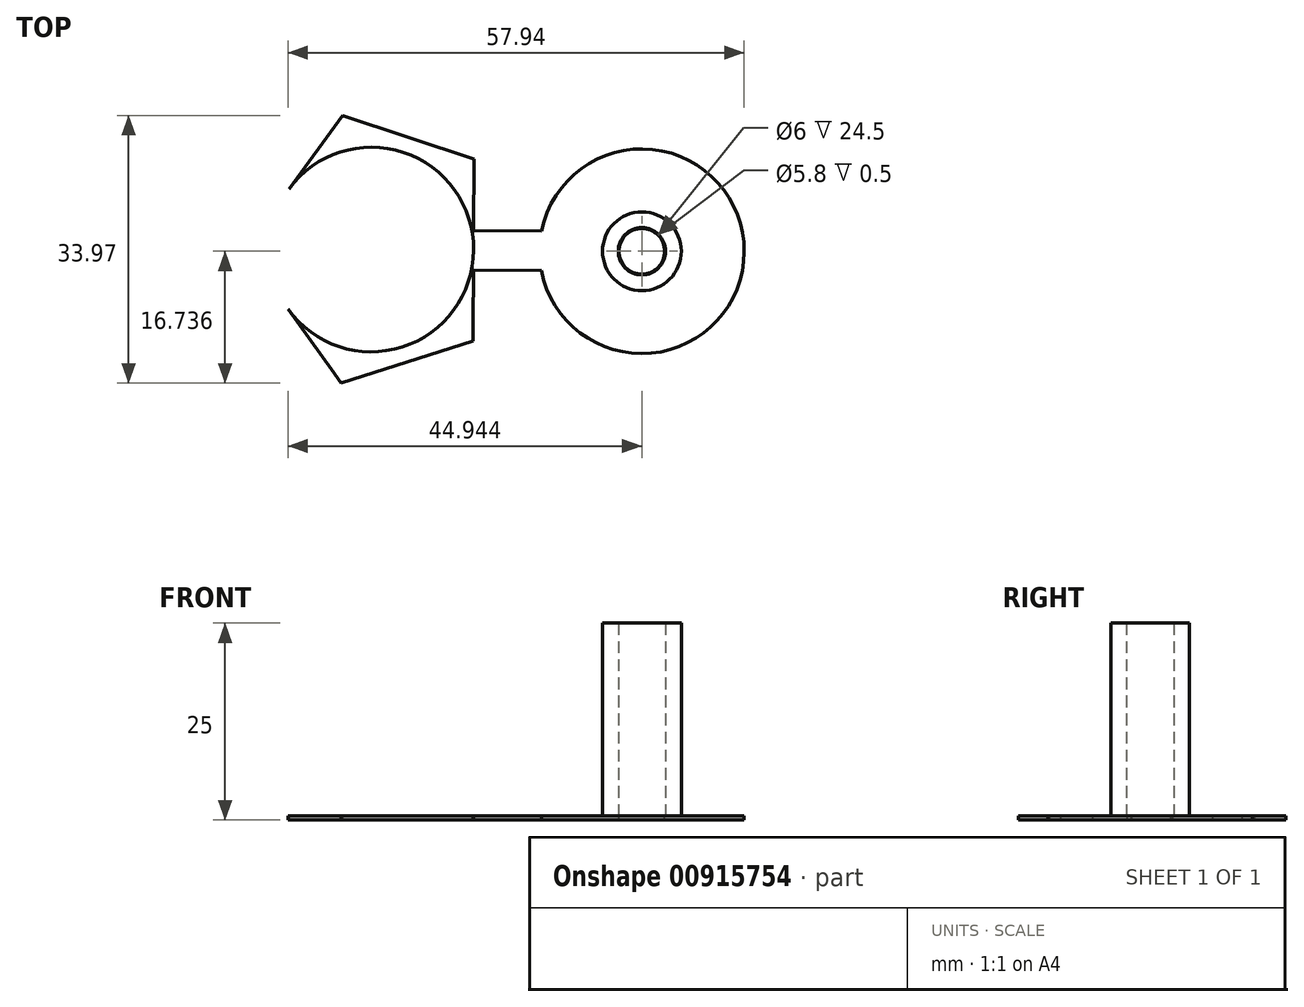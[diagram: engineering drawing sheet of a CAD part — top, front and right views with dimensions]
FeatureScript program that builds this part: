
annotation { "Feature Type Name" : "Feature", "Feature Type Description" : "" }
export const myFeature = defineFeature(function(context is Context, id is Id, definition is map)
    precondition{}
    {
        {
            var Q0;
            Q0=qCreatedBy(makeId("Top.planeOp"),FACE);
            var sketch = newSketch(context, id + "F0", { "sketchPlane" : qUnion([Q0])});
            skCircle(sketch, "E0.cCircle", {"center": v(0, 0) * mm, "radius": 13 * mm, "construction": true});
            skLineSegment(sketch, "E0.0", {"start": v(-4.87, 15.31) * mm, "end": v(13.06, 9.36) * mm});
            skLineSegment(sketch, "E0.1", {"start": v(13.06, 9.36) * mm, "end": v(12.94, -9.53) * mm});
            skLineSegment(sketch, "E0.2", {"start": v(12.94, -9.53) * mm, "end": v(-5.06, -15.25) * mm});
            skLineSegment(sketch, "E0.3", {"start": v(-5.06, -15.25) * mm, "end": v(-16.07, 0.1) * mm});
            skLineSegment(sketch, "E0.4", {"start": v(-16.07, 0.1) * mm, "end": v(-4.87, 15.31) * mm});
            skPoint(sketch, "E0.0.midPoint", {"position": v(4.1, 12.34) * mm});
            skLineSegment(sketch, "E1", {"start": v(12.74, -2.58) * mm, "end": v(34.37, -2.72) * mm});
            skLineSegment(sketch, "E2", {"start": v(34.37, -2.72) * mm, "end": v(34.37, 2.28) * mm});
            skLineSegment(sketch, "E3", {"start": v(34.37, 2.28) * mm, "end": v(12.77, 2.42) * mm});
            skLineSegment(sketch, "E4", {"start": v(0, 0) * mm, "end": v(34.37, -0.22) * mm, "construction": true});
            skCircle(sketch, "E5", {"center": v(34.37, -0.22) * mm, "radius": 13 * mm});
            skCircle(sketch, "E6", {"center": v(0, 0) * mm, "radius": 13 * mm});
            skPoint(sketch, "E7.orphan", {"position": v(0, 2.5) * mm});
            skCircle(sketch, "E8", {"center": v(34.37, -0.22) * mm, "radius": 3 * mm});
            skCircle(sketch, "E9", {"center": v(34.37, -0.22) * mm, "radius": 5 * mm});
            skSolve(sketch);
        }
        {
            var Q0;
            Q0=makeQuery(id+"F0.imprint","IMPRINT",FACE,{"disambiguationData":[TD([[makeQuery(id+"F0.imprint","IMPRINT",EDGE,{"derivedFrom":sQuery(id+"F0.wireOp",EDGE,"E5")}),1.0]])]});
            var Q1;
            {var subQ4=sQuery(id+"F0.wireOp",EDGE,"E0.0");Q1=makeQuery(id+"F0.imprint","IMPRINT",FACE,{"disambiguationData":[TD([[makeQuery(id+"F0.imprint","IMPRINT",EDGE,{"derivedFrom":subQ4}),-1.0]])]});}
            var Q2;
            {var subQ5=sQuery(id+"F0.wireOp",EDGE,"E2");Q2=makeQuery(id+"F0.imprint","IMPRINT",FACE,{"disambiguationData":[TD([[makeQuery(id+"F0.imprint","IMPRINT",EDGE,{"derivedFrom":subQ5}),1.0]])]});}
            var Q3;
            {var subQ5=sQuery(id+"F0.wireOp",EDGE,"jRpVBXlm-WpGf-nScz-VXjb-NFzC1IAMgS5t");Q3=makeQuery(id+"F0.imprint","IMPRINT",FACE,{"disambiguationData":[TD([[makeQuery(id+"F0.imprint","IMPRINT",EDGE,{"derivedFrom":subQ5}),1.0]])]});}
            var Q4;
            {var subQ0=sQuery(id+"F0.wireOp",EDGE,"E0.2");var subQ1=sQuery(id+"F0.wireOp",EDGE,"E0.1");var subQ2=makeQuery(id+"F0.imprint","INTERSECT",VERTEX,{"derivedFrom":[subQ1,subQ0]});Q4=makeQuery(id+"F0.imprint","IMPRINT",FACE,{"disambiguationData":[TD([[makeQuery(id+"F0.imprint","IMPRINT",EDGE,{"disambiguationData":[TD([[subQ2,1.0]])],"derivedFrom":subQ1}),-1.0]])]});}
            var Q5;
            {var subQ0=sQuery(id+"F0.wireOp",EDGE,"E3");var subQ1=sQuery(id+"F0.wireOp",EDGE,"E0.1");var subQ2=makeQuery(id+"F0.imprint","INTERSECT",VERTEX,{"derivedFrom":[subQ1,subQ0]});Q5=makeQuery(id+"F0.imprint","IMPRINT",FACE,{"disambiguationData":[TD([[makeQuery(id+"F0.imprint","IMPRINT",EDGE,{"disambiguationData":[TD([[subQ2,-1.0]])],"derivedFrom":subQ1}),-1.0]])]});}
            var Q6;
            {var subQ0=sQuery(id+"F0.wireOp",EDGE,"E0.1");var subQ1=sQuery(id+"F0.wireOp",EDGE,"E0.0");var subQ2=makeQuery(id+"F0.imprint","INTERSECT",VERTEX,{"derivedFrom":[subQ1,subQ0]});Q6=makeQuery(id+"F0.imprint","IMPRINT",FACE,{"disambiguationData":[TD([[makeQuery(id+"F0.imprint","IMPRINT",EDGE,{"disambiguationData":[TD([[subQ2,1.0]])],"derivedFrom":subQ1}),-1.0]])]});}
            var Q7;
            {var subQ2=sQuery(id+"F0.wireOp",EDGE,"E1");var subQ4=sQuery(id+"F0.wireOp",EDGE,"TUE00Eo4-W1ab-wloH-Eorr-XZJXafVs9wpa.left");var subQ8=makeQuery(id+"F0.imprint","INTERSECT",VERTEX,{"derivedFrom":[subQ2,subQ4]});Q7=makeQuery(id+"F0.imprint","IMPRINT",FACE,{"disambiguationData":[TD([[makeQuery(id+"F0.imprint","IMPRINT",EDGE,{"disambiguationData":[TD([[subQ8,-1.0]])],"derivedFrom":subQ2}),-1.0]])]});}
            var Q8;
            {var subQ0=sQuery(id+"F0.wireOp",EDGE,"TUE00Eo4-W1ab-wloH-Eorr-XZJXafVs9wpa.top");var subQ1=sQuery(id+"F0.wireOp",EDGE,"E0.1");var subQ2=makeQuery(id+"F0.imprint","INTERSECT",VERTEX,{"derivedFrom":[subQ1,subQ0]});Q8=makeQuery(id+"F0.imprint","IMPRINT",FACE,{"disambiguationData":[TD([[makeQuery(id+"F0.imprint","IMPRINT",EDGE,{"disambiguationData":[TD([[subQ2,1.0]])],"derivedFrom":subQ1}),-1.0]])]});}
            var Q9;
            {var subQ0=sQuery(id+"F0.wireOp",EDGE,"TUE00Eo4-W1ab-wloH-Eorr-XZJXafVs9wpa.bottom");Q9=makeQuery(id+"F0.imprint","IMPRINT",FACE,{"disambiguationData":[TD([[makeQuery(id+"F0.imprint","IMPRINT",EDGE,{"derivedFrom":subQ0}),-1.0]])]});}
            var Q10;
            {var subQ0=sQuery(id+"F0.wireOp",EDGE,"E3");var subQ1=sQuery(id+"F0.wireOp",EDGE,"E0.1");var subQ2=makeQuery(id+"F0.imprint","INTERSECT",VERTEX,{"derivedFrom":[subQ1,subQ0]});Q10=makeQuery(id+"F0.imprint","IMPRINT",FACE,{"disambiguationData":[TD([[makeQuery(id+"F0.imprint","IMPRINT",EDGE,{"disambiguationData":[TD([[subQ2,-1.0]])],"derivedFrom":subQ1}),1.0]])]});}
            var Q11;
            {var subQ0=sQuery(id+"F0.wireOp",EDGE,"E0.3");var subQ1=sQuery(id+"F0.wireOp",EDGE,"E0.2");var subQ2=makeQuery(id+"F0.imprint","INTERSECT",VERTEX,{"derivedFrom":[subQ1,subQ0]});Q11=makeQuery(id+"F0.imprint","IMPRINT",FACE,{"disambiguationData":[TD([[makeQuery(id+"F0.imprint","IMPRINT",EDGE,{"disambiguationData":[TD([[subQ2,1.0]])],"derivedFrom":subQ1}),-1.0]])]});}
            var Q12;
            {var subQ0=sQuery(id+"F0.wireOp",EDGE,"E9");var subQ1=sQuery(id+"F0.wireOp",EDGE,"E1");var subQ2=makeQuery(id+"F0.imprint","INTERSECT",VERTEX,{"derivedFrom":[subQ1,subQ0]});Q12=makeQuery(id+"F0.imprint","IMPRINT",FACE,{"disambiguationData":[TD([[makeQuery(id+"F0.imprint","IMPRINT",EDGE,{"disambiguationData":[TD([[subQ2,-1.0]])],"derivedFrom":subQ1}),1.0]])]});}
            extrude(context, id + "F1", {"entities" : qUnion([Q0, Q1, Q2, Q3, Q4, Q5, Q6, Q7, Q8, Q9, Q10, Q11, Q12]), "depth" : .5 * mm, "offsetDistance" : 25 * mm});
        }
        {
            var Q0;
            {var subQ0=sQuery(id+"F0.wireOp",EDGE,"E9");var subQ1=sQuery(id+"F0.wireOp",EDGE,"E1");var subQ2=makeQuery(id+"F0.imprint","INTERSECT",VERTEX,{"derivedFrom":[subQ1,subQ0]});Q0=makeQuery(id+"F0.imprint","IMPRINT",FACE,{"disambiguationData":[TD([[makeQuery(id+"F0.imprint","IMPRINT",EDGE,{"disambiguationData":[TD([[subQ2,-1.0]])],"derivedFrom":subQ1}),-1.0]])]});}
            var Q1;
            {var subQ0=sQuery(id+"F0.wireOp",EDGE,"E9");var subQ1=sQuery(id+"F0.wireOp",EDGE,"E1");var subQ2=makeQuery(id+"F0.imprint","INTERSECT",VERTEX,{"derivedFrom":[subQ1,subQ0]});Q1=makeQuery(id+"F0.imprint","IMPRINT",FACE,{"disambiguationData":[TD([[makeQuery(id+"F0.imprint","IMPRINT",EDGE,{"disambiguationData":[TD([[subQ2,-1.0]])],"derivedFrom":subQ1}),1.0]])]});}
            extrude(context, id + "F2", {"entities" : qUnion([Q0, Q1]), "operationType" : NewBodyOperationType.ADD, "depth" : 25 * mm, "offsetDistance" : 25 * mm});
        }
        {
            var Q0;
            Q0=makeQuery(id+"F1.opExtrude","CAP_FACE",FACE,{"disambiguationData":[OSD([sQuery(id+"F0.wireOp",EDGE,"E0.0"),sQuery(id+"F0.wireOp",EDGE,"E0.1"),sQuery(id+"F0.wireOp",EDGE,"E0.2"),sQuery(id+"F0.wireOp",EDGE,"E1"),sQuery(id+"F0.wireOp",EDGE,"E3"),sQuery(id+"F0.wireOp",EDGE,"E5"),sQuery(id+"F0.wireOp",EDGE,"E6")])],"isStart":false});
            var sketch = newSketch(context, id + "F3", { "sketchPlane" : qUnion([Q0])});
            skCircle(sketch, "E10", {"center": v(34.37, -0.22) * mm, "radius": 2.9 * mm});
            skSolve(sketch);
        }
        {
            var Q0;
            Q0=makeQuery(id+"F3.imprint","IMPRINT",FACE,{"disambiguationData":[TD([[makeQuery(id+"F3.imprint","IMPRINT",EDGE,{"derivedFrom":sQuery(id+"F3.wireOp",EDGE,"E10")}),1.0]])]});
            extrude(context, id + "F4", {"entities" : qUnion([Q0]), "operationType" : NewBodyOperationType.REMOVE, "endBound" : BoundingType.THROUGH_ALL, "oppositeDirection" : true, "depth" : 25 * mm, "offsetDistance" : 25 * mm});
        }
        {
            var Q0;
            {var subQ0=sQuery(id+"F0.wireOp",EDGE,"E0.1");var subQ1=sQuery(id+"F0.wireOp",EDGE,"E0.0");var subQ2=makeQuery(id+"F0.imprint","INTERSECT",VERTEX,{"derivedFrom":[subQ1,subQ0]});Q0=makeQuery(id+"F0.imprint","IMPRINT",FACE,{"disambiguationData":[TD([[makeQuery(id+"F0.imprint","IMPRINT",EDGE,{"disambiguationData":[TD([[subQ2,1.0]])],"derivedFrom":subQ1}),-1.0]])]});}
            var sketch = newSketch(context, id + "F5", { "sketchPlane" : qUnion([Q0])});
            skArc(sketch, "E11.0.0", {"start": v(-10.47, 7.7) * mm, "mid": v(-3.94, 12.39) * mm, "end": v(4.1, 12.34) * mm});
            skLineSegment(sketch, "E11.0.1", {"start": v(4.1, 12.34) * mm, "end": v(-4.87, 15.31) * mm});
            skLineSegment(sketch, "E11.0.2", {"start": v(-4.87, 15.31) * mm, "end": v(-10.47, 7.7) * mm});
            skArc(sketch, "E12.0.0", {"start": v(4.1, 12.34) * mm, "mid": v(9.79, 8.56) * mm, "end": v(12.77, 2.42) * mm});
            skLineSegment(sketch, "E12.0.1", {"start": v(12.77, 2.42) * mm, "end": v(13.02, 2.42) * mm});
            skLineSegment(sketch, "E12.0.2", {"start": v(13.02, 2.42) * mm, "end": v(13.06, 9.36) * mm});
            skLineSegment(sketch, "E12.0.3", {"start": v(13.06, 9.36) * mm, "end": v(4.1, 12.34) * mm});
            skLineSegment(sketch, "E13", {"start": v(-4.87, 15.31) * mm, "end": v(-3.62, 17) * mm});
            skLineSegment(sketch, "E14", {"start": v(-3.62, 17) * mm, "end": v(13.07, 11.46) * mm});
            skLineSegment(sketch, "E15", {"start": v(13.07, 11.46) * mm, "end": v(13.06, 9.36) * mm});
            skLineSegment(sketch, "E16.MirrorCS", {"start": v(-3.84, -16.96) * mm, "end": v(12.92, -11.63) * mm});
            skLineSegment(sketch, "E17.MirrorCS", {"start": v(-5.07, -15.25) * mm, "end": v(-3.84, -16.96) * mm});
            skLineSegment(sketch, "E18.MirrorCS", {"start": v(12.92, -11.63) * mm, "end": v(12.94, -9.53) * mm});
            skArc(sketch, "E19.0.0", {"start": v(3.94, -12.39) * mm, "mid": v(-4.1, -12.34) * mm, "end": v(-10.57, -7.57) * mm});
            skLineSegment(sketch, "E19.0.1", {"start": v(-10.57, -7.57) * mm, "end": v(-5.06, -15.25) * mm});
            skLineSegment(sketch, "E19.0.2", {"start": v(-5.06, -15.25) * mm, "end": v(3.94, -12.39) * mm});
            skLineSegment(sketch, "E20.0.0", {"start": v(12.98, -2.58) * mm, "end": v(12.74, -2.58) * mm});
            skArc(sketch, "E20.0.1", {"start": v(12.74, -2.58) * mm, "mid": v(9.67, -8.68) * mm, "end": v(3.94, -12.39) * mm});
            skLineSegment(sketch, "E20.0.2", {"start": v(3.94, -12.39) * mm, "end": v(12.94, -9.53) * mm});
            skLineSegment(sketch, "E20.0.3", {"start": v(12.94, -9.53) * mm, "end": v(12.98, -2.58) * mm});
            skLineSegment(sketch, "E21", {"start": v(12.94, -9.53) * mm, "end": v(-5.06, -15.25) * mm});
            skLineSegment(sketch, "E22", {"start": v(-5.06, -15.25) * mm, "end": v(12.94, -9.53) * mm});
            skLineSegment(sketch, "E23", {"start": v(12.92, -11.63) * mm, "end": v(-3.84, -16.96) * mm});
            skLineSegment(sketch, "E24", {"start": v(-3.84, -16.96) * mm, "end": v(-5.06, -15.25) * mm});
            skSolve(sketch);
        }
        {
            var Q0;
            Q0=makeQuery(id+"F5.imprint","IMPRINT",FACE,{"disambiguationData":[TD([[makeQuery(id+"F5.imprint","IMPRINT",EDGE,{"derivedFrom":sQuery(id+"F5.wireOp",EDGE,"E11.0.1")}),-1.0]])]});
            var Q1;
            {var subQ0=sQuery(id+"F5.wireOp",EDGE,"E18.MirrorCS");Q1=makeQuery(id+"F5.imprint","IMPRINT",FACE,{"disambiguationData":[TD([[makeQuery(id+"F5.imprint","IMPRINT",EDGE,{"derivedFrom":subQ0}),1.0]])]});}
            var Q2;
            Q2=makeQuery(id+"F1.opExtrude","CAP_FACE",FACE,{"disambiguationData":[OSD([sQuery(id+"F0.wireOp",EDGE,"E0.0"),sQuery(id+"F0.wireOp",EDGE,"E0.1"),sQuery(id+"F0.wireOp",EDGE,"E0.2"),sQuery(id+"F0.wireOp",EDGE,"E1"),sQuery(id+"F0.wireOp",EDGE,"E3"),sQuery(id+"F0.wireOp",EDGE,"E5"),sQuery(id+"F0.wireOp",EDGE,"E6")])],"isStart":false});
            extrude(context, id + "F6", {"entities" : qUnion([Q0, Q1]), "operationType" : NewBodyOperationType.ADD, "endBound" : BoundingType.UP_TO_SURFACE, "depth" : 25 * mm, "endBoundEntityFace" : qUnion([Q2]), "offsetDistance" : 25 * mm});
        }
    });
